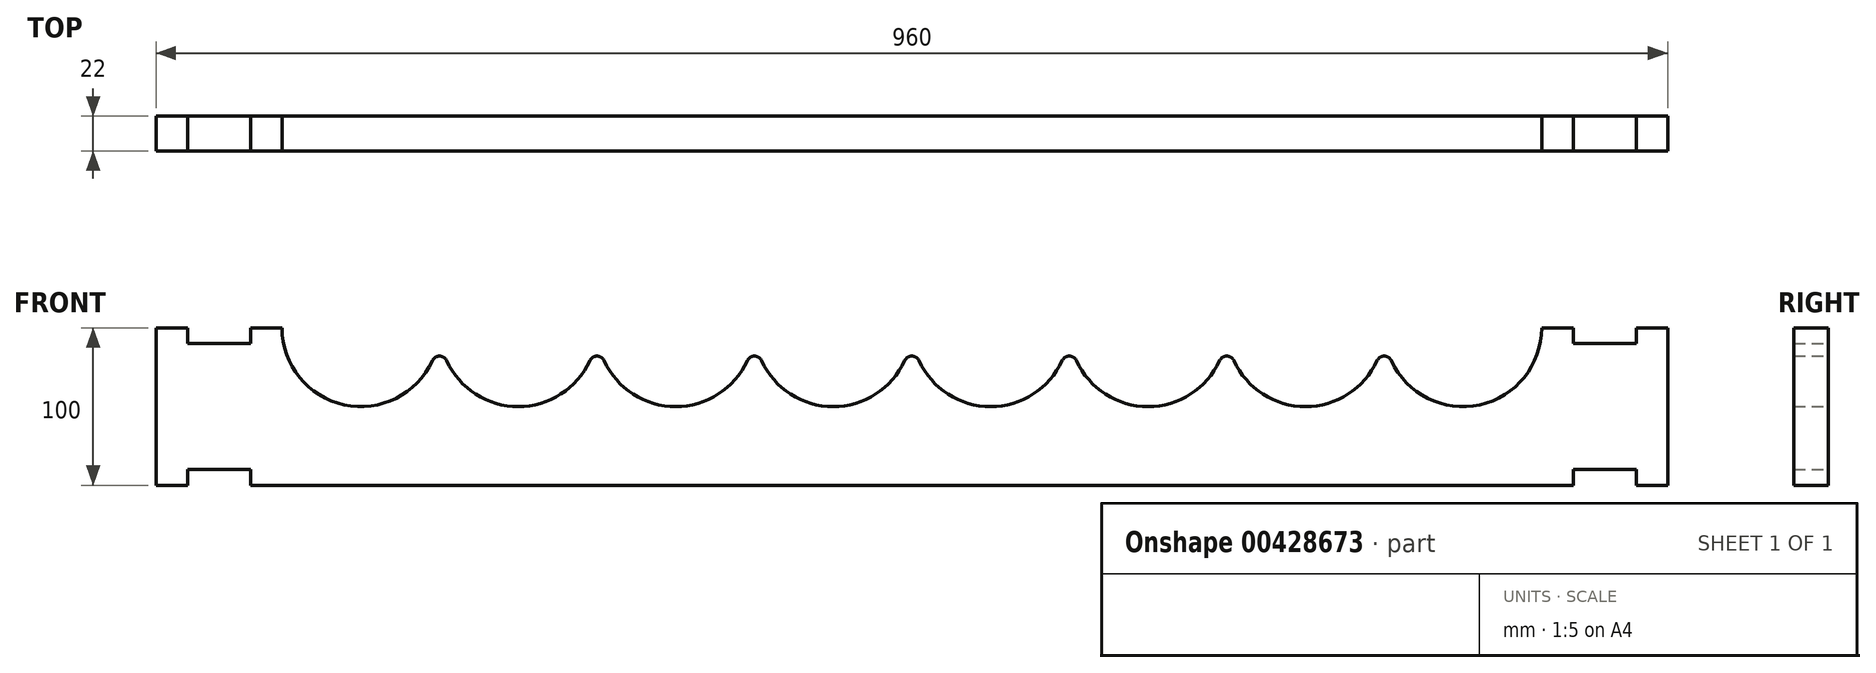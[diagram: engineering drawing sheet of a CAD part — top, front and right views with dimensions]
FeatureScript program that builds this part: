
annotation { "Feature Type Name" : "Feature", "Feature Type Description" : "" }
export const myFeature = defineFeature(function(context is Context, id is Id, definition is map)
    precondition{}
    {
        {
            var Q0;
            Q0=qCreatedBy(makeId("Front.planeOp"),FACE);
            var sketch = newSketch(context, id + "F0", { "sketchPlane" : qUnion([Q0])});
            skLineSegment(sketch, "E0.bottom", {"start": v(480, -50) * mm, "end": v(460, -50) * mm});
            skLineSegment(sketch, "E0.top", {"start": v(480, 50) * mm, "end": v(460, 50) * mm});
            skPoint(sketch, "E0.middle", {"position": v(0, 0) * mm});
            skArc(sketch, "E1", {"start": v(4.55, 29.17) * mm, "mid": v(50, 0) * mm, "end": v(95.45, 29.17) * mm});
            skArc(sketch, "E2", {"start": v(104.55, 29.17) * mm, "mid": v(150, 0) * mm, "end": v(195.45, 29.17) * mm});
            skArc(sketch, "E3", {"start": v(204.55, 29.17) * mm, "mid": v(250, 0) * mm, "end": v(295.45, 29.17) * mm});
            skArc(sketch, "E4", {"start": v(304.55, 29.17) * mm, "mid": v(360.66, 1.15) * mm, "end": v(400, 50) * mm});
            skArc(sketch, "E5", {"start": v(-95.45, 29.17) * mm, "mid": v(-50, 0) * mm, "end": v(-4.55, 29.17) * mm});
            skArc(sketch, "E6", {"start": v(-195.45, 29.17) * mm, "mid": v(-150, 0) * mm, "end": v(-104.55, 29.17) * mm});
            skArc(sketch, "E7", {"start": v(-295.45, 29.17) * mm, "mid": v(-250, 0) * mm, "end": v(-204.55, 29.17) * mm});
            skArc(sketch, "E8", {"start": v(-400, 50) * mm, "mid": v(-360.66, 1.15) * mm, "end": v(-304.55, 29.17) * mm});
            skLineSegment(sketch, "E9.trimOffspring", {"start": v(-400, 50) * mm, "end": v(-420, 50) * mm});
            skPoint(sketch, "E10.visualSharp", {"position": v(-300, 50) * mm});
            skArc(sketch, "E10.filletArc", {"start": v(-295.45, 29.17) * mm, "mid": v(-300, 32.09) * mm, "end": v(-304.55, 29.17) * mm});
            skPoint(sketch, "E11.visualSharp", {"position": v(-200, 50) * mm});
            skArc(sketch, "E11.filletArc", {"start": v(-195.45, 29.17) * mm, "mid": v(-200, 32.09) * mm, "end": v(-204.55, 29.17) * mm});
            skPoint(sketch, "E12.visualSharp", {"position": v(-100, 50) * mm});
            skArc(sketch, "E12.filletArc", {"start": v(-95.45, 29.17) * mm, "mid": v(-100, 32.09) * mm, "end": v(-104.55, 29.17) * mm});
            skPoint(sketch, "E13.visualSharp", {"position": v(0, 50) * mm});
            skArc(sketch, "E13.filletArc", {"start": v(4.55, 29.17) * mm, "mid": v(0, 32.09) * mm, "end": v(-4.55, 29.17) * mm});
            skPoint(sketch, "E14.visualSharp", {"position": v(100, 50) * mm});
            skArc(sketch, "E14.filletArc", {"start": v(104.55, 29.17) * mm, "mid": v(100, 32.09) * mm, "end": v(95.45, 29.17) * mm});
            skPoint(sketch, "E15.visualSharp", {"position": v(200, 50) * mm});
            skArc(sketch, "E15.filletArc", {"start": v(204.55, 29.17) * mm, "mid": v(200, 32.09) * mm, "end": v(195.45, 29.17) * mm});
            skPoint(sketch, "E16.visualSharp", {"position": v(300, 50) * mm});
            skArc(sketch, "E16.filletArc", {"start": v(304.55, 29.17) * mm, "mid": v(300, 32.09) * mm, "end": v(295.45, 29.17) * mm});
            skLineSegment(sketch, "E17", {"start": v(-460, 50) * mm, "end": v(-480, 50) * mm});
            skLineSegment(sketch, "E18", {"start": v(-480, 50) * mm, "end": v(-480, -50) * mm});
            skLineSegment(sketch, "E19", {"start": v(-480, -50) * mm, "end": v(-460, -50) * mm});
            skLineSegment(sketch, "E20", {"start": v(-420, -50) * mm, "end": v(-420, -40) * mm});
            skLineSegment(sketch, "E21", {"start": v(-420, 40) * mm, "end": v(-420, 50) * mm});
            skLineSegment(sketch, "E22", {"start": v(-460, -50) * mm, "end": v(-460, -40) * mm});
            skLineSegment(sketch, "E23", {"start": v(-460, -40) * mm, "end": v(-420, -40) * mm});
            skLineSegment(sketch, "E24", {"start": v(-460, 50) * mm, "end": v(-460, 40) * mm});
            skLineSegment(sketch, "E25", {"start": v(-460, 40) * mm, "end": v(-420, 40) * mm});
            skLineSegment(sketch, "E26", {"start": v(400, 50) * mm, "end": v(420, 50) * mm});
            skLineSegment(sketch, "E27", {"start": v(460, 50) * mm, "end": v(480, 50) * mm});
            skLineSegment(sketch, "E28", {"start": v(460, 50) * mm, "end": v(460, 40) * mm});
            skLineSegment(sketch, "E29", {"start": v(460, -40) * mm, "end": v(460, -50) * mm});
            skLineSegment(sketch, "E30", {"start": v(420, 50) * mm, "end": v(420, 40) * mm});
            skLineSegment(sketch, "E31", {"start": v(420, 40) * mm, "end": v(460, 40) * mm});
            skLineSegment(sketch, "E32", {"start": v(420, -50) * mm, "end": v(420, -40) * mm});
            skLineSegment(sketch, "E33", {"start": v(420, -40) * mm, "end": v(460, -40) * mm});
            skLineSegment(sketch, "E34", {"start": v(480, 50) * mm, "end": v(480, -50) * mm});
            skLineSegment(sketch, "E35.trimOffspring", {"start": v(420, 50) * mm, "end": v(400, 50) * mm});
            skLineSegment(sketch, "E36.trimOffspring", {"start": v(420, -50) * mm, "end": v(-420, -50) * mm});
            skSolve(sketch);
        }
        {
            var Q0;
            Q0 = qSketchRegion(id + "F0", true);
            extrude(context, id + "F1", {"entities" : qUnion([Q0]), "depth" : 22 * mm});
        }
    });
